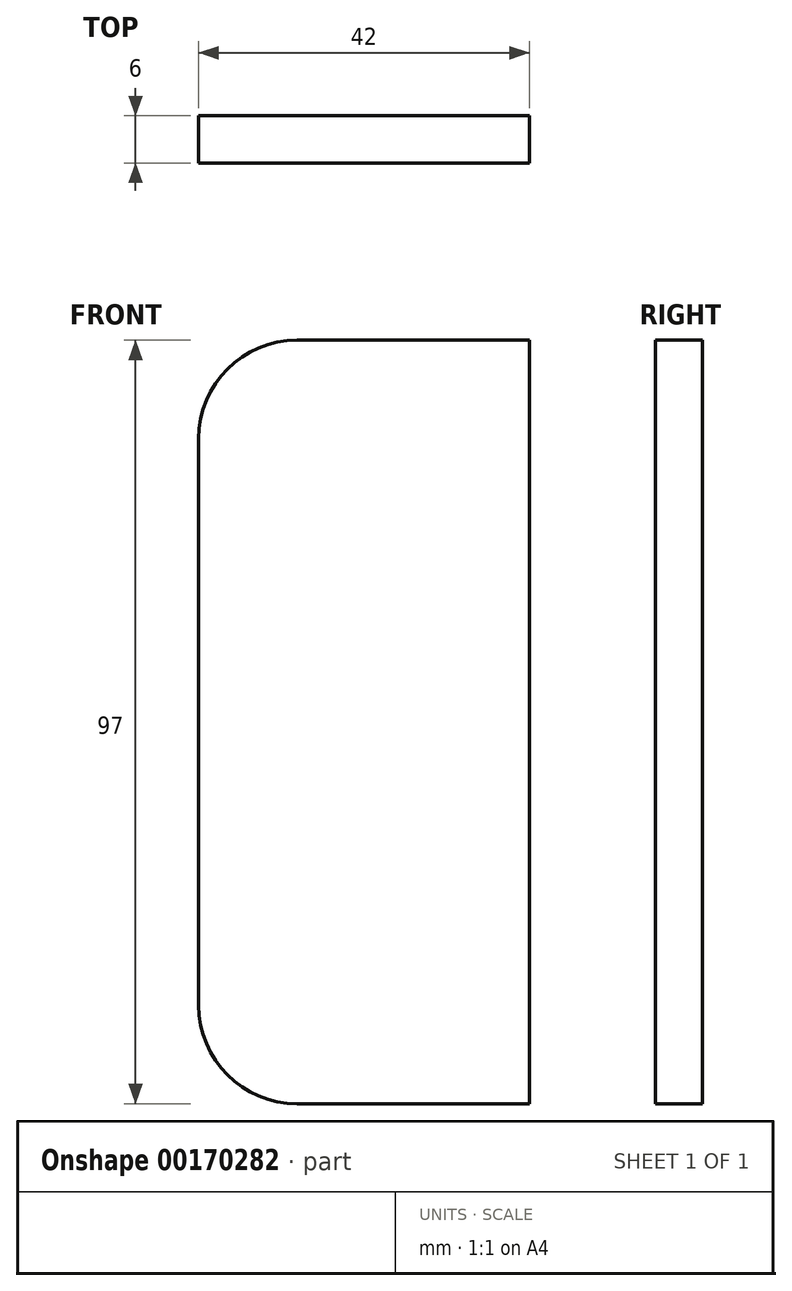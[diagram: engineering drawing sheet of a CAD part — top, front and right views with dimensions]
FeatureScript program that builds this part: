
annotation { "Feature Type Name" : "Feature", "Feature Type Description" : "" }
export const myFeature = defineFeature(function(context is Context, id is Id, definition is map)
    precondition{}
    {
        {
            var Q0;
            Q0=qCreatedBy(makeId("Front.planeOp"),FACE);
            var sketch = newSketch(context, id + "F0", { "sketchPlane" : qUnion([Q0])});
            skLineSegment(sketch, "E0.bottom", {"start": v(21, 48.5) * mm, "end": v(-8.5, 48.5) * mm});
            skLineSegment(sketch, "E0.top", {"start": v(21, -48.5) * mm, "end": v(-8.5, -48.5) * mm});
            skLineSegment(sketch, "E0.left", {"start": v(21, 48.5) * mm, "end": v(21, -48.5) * mm});
            skLineSegment(sketch, "E0.right", {"start": v(-21, 36) * mm, "end": v(-21, -36) * mm});
            skPoint(sketch, "E0.middle", {"position": v(0, 0) * mm});
            skPoint(sketch, "E1.visualSharp", {"position": v(-21, 48.5) * mm});
            skArc(sketch, "E1.filletArc", {"start": v(-8.5, 48.5) * mm, "mid": v(-17.34, 44.84) * mm, "end": v(-21, 36) * mm});
            skPoint(sketch, "E2.visualSharp", {"position": v(-21, -48.5) * mm});
            skArc(sketch, "E2.filletArc", {"start": v(-21, -36) * mm, "mid": v(-17.34, -44.84) * mm, "end": v(-8.5, -48.5) * mm});
            skSolve(sketch);
        }
        {
            var Q0;
            Q0 = qSketchRegion(id + "F0", true);
            extrude(context, id + "F1", {"entities" : qUnion([Q0]), "depth" : 6 * mm});
        }
    });
